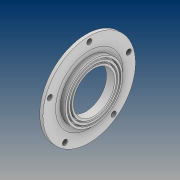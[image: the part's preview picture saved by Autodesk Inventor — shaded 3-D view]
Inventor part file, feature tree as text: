
AUTODESK INVENTOR PART (.ipt)
format: ipt  version: 2021 (Build 250183000, 183)  size: 214,016 bytes
history: native  units: mm
features: thread x5, sketch x3, revolve x2, extrude x1
ambient origin geometry x8: Origin, YZ Plane, XZ Plane, XY Plane, X Axis, Y Axis, Z Axis, Center Point
bodies: Solid1 (feature_tree)
feature tree (11):
  extrude  "Extrusion1"  Depth=230.0mm
  revolve  "Revolution1"  [1 undecoded]
  revolve  "Revolution2"  Angle=90.0deg
  thread  "Thread7"  [1 undecoded]
  thread  "Thread8"  [1 undecoded]
  thread  "Thread9"  [1 undecoded]
  thread  "Thread10"  [1 undecoded]
  thread  "Thread11"  [1 undecoded]
  sketch  "Sketch1"  dims[d0=290.0mm d1=230.0mm]
  sketch  "Sketch2"  dims[d2=260.0mm d3=16.0mm]
  sketch  "Sketch3"  dims[d8=10.0mm d9=0.0mm d22=90.0deg d23=90.0deg d24=50.0mm d26=360.0deg d28=10.0mm d29=0.0mm d30=10.0mm d31=0.0mm d32=10.0mm d33=0.0mm d34=10.0mm d35=0.0mm d36=10.0mm d37=0.0mm]
note: 6 required parameter values undecoded (feature->parameter linkage not recoverable at this tier; creation-order binding heuristic only, values carry confidence <= 0.55)